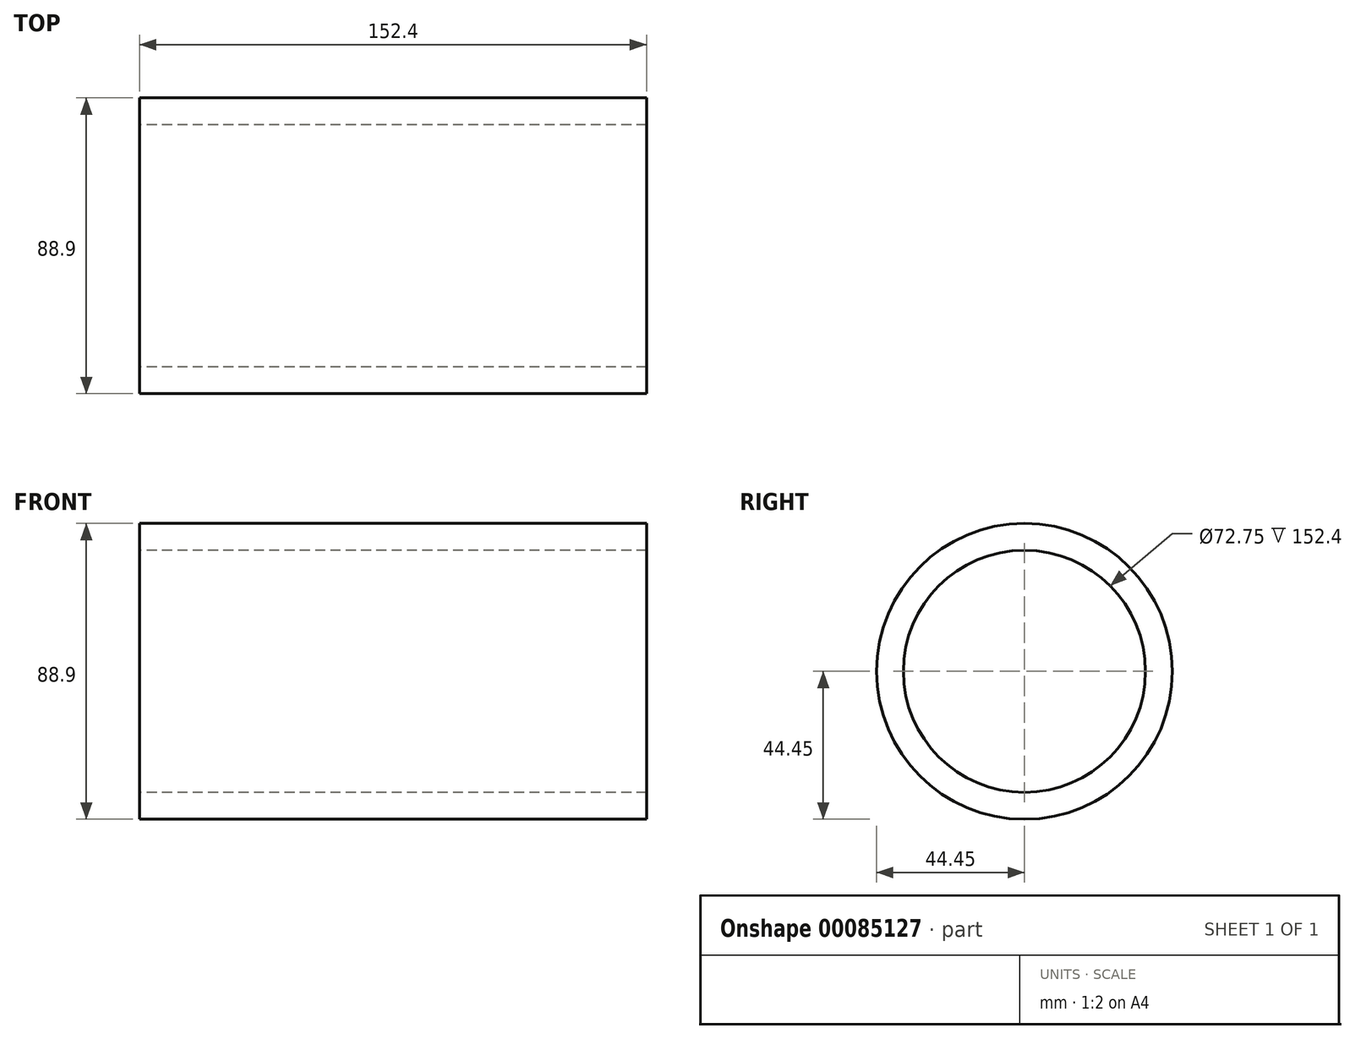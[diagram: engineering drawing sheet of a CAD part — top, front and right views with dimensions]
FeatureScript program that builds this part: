
annotation { "Feature Type Name" : "Feature", "Feature Type Description" : "" }
export const myFeature = defineFeature(function(context is Context, id is Id, definition is map)
    precondition{}
    {
        {
            var Q0;
            Q0=qCreatedBy(makeId("Right.planeOp"),FACE);
            var sketch = newSketch(context, id + "F0", { "sketchPlane" : qUnion([Q0])});
            skCircle(sketch, "E0", {"center": v(0, 0) * mm, "radius": 44.45 * mm});
            skCircle(sketch, "E1", {"center": v(0, 0) * mm, "radius": 36.37 * mm});
            skSolve(sketch);
        }
        {
            var Q0;
            Q0=makeQuery(id+"F0.imprint","IMPRINT",FACE,{"disambiguationData":[TD([[makeQuery(id+"F0.imprint","IMPRINT",EDGE,{"derivedFrom":sQuery(id+"F0.wireOp",EDGE,"E0")}),1.0]])]});
            extrude(context, id + "F1", {"entities" : qUnion([Q0]), "depth" : 152.4 * mm});
        }
    });
